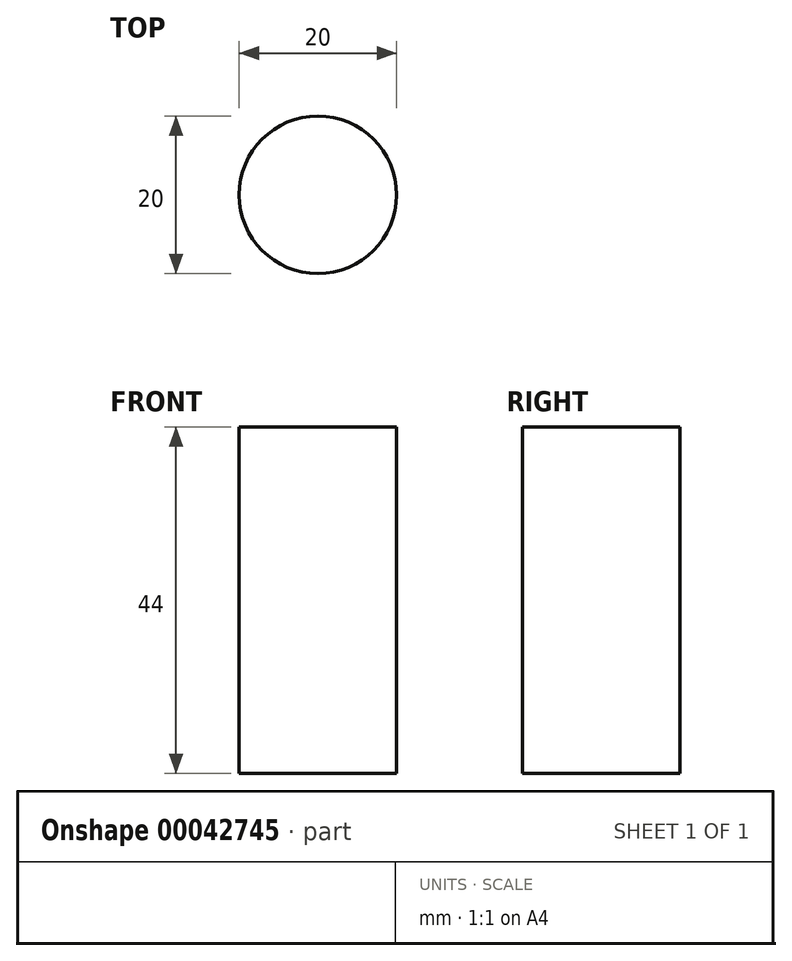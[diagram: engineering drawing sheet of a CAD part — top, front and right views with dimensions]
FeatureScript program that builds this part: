
annotation { "Feature Type Name" : "Feature", "Feature Type Description" : "" }
export const myFeature = defineFeature(function(context is Context, id is Id, definition is map)
    precondition{}
    {
        {
            var Q0;
            Q0=qCreatedBy(makeId("Top.planeOp"),FACE);
            var sketch = newSketch(context, id + "F0", { "sketchPlane" : qUnion([Q0])});
            skCircle(sketch, "E0", {"center": v(0, 0) * mm, "radius": 10 * mm});
            skSolve(sketch);
        }
        {
            var Q0;
            Q0 = qSketchRegion(id + "F0", true);
            extrude(context, id + "F1", {"entities" : qUnion([Q0]), "depth" : 44 * mm});
        }
    });
